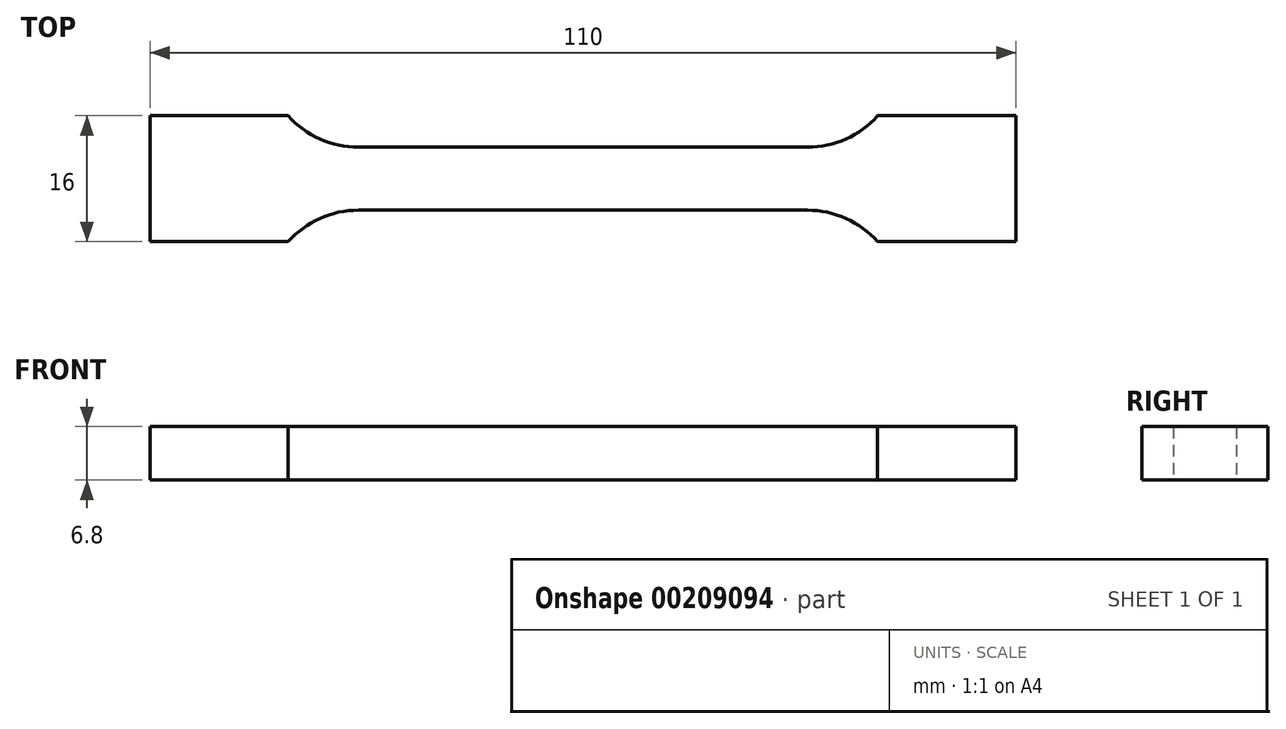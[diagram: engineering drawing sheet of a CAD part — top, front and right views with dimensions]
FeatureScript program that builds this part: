
annotation { "Feature Type Name" : "Feature", "Feature Type Description" : "" }
export const myFeature = defineFeature(function(context is Context, id is Id, definition is map)
    precondition{}
    {
        {
            var Q0;
            Q0=qCreatedBy(makeId("Top.planeOp"),FACE);
            var sketch = newSketch(context, id + "F0", { "sketchPlane" : qUnion([Q0])});
            skLineSegment(sketch, "E0.left", {"start": v(55, -8) * mm, "end": v(55, 8) * mm});
            skLineSegment(sketch, "E0.right", {"start": v(-55, -8) * mm, "end": v(-55, 8) * mm});
            skLineSegment(sketch, "E1.bottom", {"start": v(28.5, -4) * mm, "end": v(-28.5, -4) * mm});
            skLineSegment(sketch, "E1.top", {"start": v(28.5, 4) * mm, "end": v(-28.5, 4) * mm});
            skPoint(sketch, "E1.middle", {"position": v(0, 0) * mm});
            skArc(sketch, "E2", {"start": v(-28.5, 4) * mm, "mid": v(-33.4, 5.05) * mm, "end": v(-37.44, 8) * mm});
            skArc(sketch, "E3", {"start": v(28.5, 4) * mm, "mid": v(33.4, 5.05) * mm, "end": v(37.44, 8) * mm});
            skArc(sketch, "E4", {"start": v(-28.5, -4) * mm, "mid": v(-33.4, -5.05) * mm, "end": v(-37.44, -8) * mm});
            skArc(sketch, "E5", {"start": v(28.5, -4) * mm, "mid": v(33.4, -5.05) * mm, "end": v(37.44, -8) * mm});
            skLineSegment(sketch, "E6", {"start": v(-55, 8) * mm, "end": v(-37.44, 8) * mm});
            skLineSegment(sketch, "E7", {"start": v(37.44, 8) * mm, "end": v(55, 8) * mm});
            skLineSegment(sketch, "E8", {"start": v(55, -8) * mm, "end": v(37.44, -8) * mm});
            skLineSegment(sketch, "E9", {"start": v(-37.44, -8) * mm, "end": v(-55, -8) * mm});
            skSolve(sketch);
        }
        {
            var Q0;
            Q0=qSketchRegion(id+"F0",true);
            var Q1;
            Q1=makeQuery(id+"F0.imprint","IMPRINT",FACE,{"disambiguationData":[TD([[makeQuery(id+"F0.imprint","IMPRINT",EDGE,{"derivedFrom":sQuery(id+"F0.wireOp",EDGE,"E0.left")}),1.0]])]});
            extrude(context, id + "F1", {"entities" : qUnion([Q0, Q1]), "depth" : 6.8 * mm, "symmetric" : true});
        }
    });
